# Revit family: pefy-p22_36mlg9(-r)_50Hz
name_source: partatom
category: 機械設備
units: mm (PartAtom-declared; Revit-internal decimal feet)

## family parameters
OmniClass タイトル = Split System Air Conditioning Units
OmniClass 番号 = 23.75.10.24.21.27.27
パーツ タイプ = 標準
ロード時にボイドで切り取り = いいえ
丸型コネクタ寸法 = 直径を使用
作業面ベース = いいえ
共有 = いいえ
常に垂直 = はい
部屋計算ポイント = はい

## types (6) — shared parameters
Depth = 550  [stored 1.80446 ft]
Height = 300  [stored 0.984252 ft]
IfcExportAs = IfcUnitaryEquipmentType
IfcExportType = AIRCONDITIONINGUNIT
MID風量 = 348.0 m³/h
MIN風量 = 288.0 m³/h
OmniClassCode = 23-33 17 13 11
URL = https://www.mitsubishielectric.co.jp
Uniclass2015Code = Pr_70_65_03_84
Uniclass2015Title = Split coil remote air cooled condensing units
Uniclass2015Version = Systems v1.9
Width = 530  [stored 1.73885 ft]
ドレン管径 = 27.20 mm
仕様書バージョン = Version1.0
企業コード = 108420
冷媒ガス管径 = 12.70 mm
冷媒液管径 = 6.35 mm
冷媒管径 = 100.00 mm
冷媒管径符号 = Ac
冷媒高低圧ガス管径 = 0.00 mm
分類コード = 50053003221070
加湿給水管径 = 0.00 mm
参照している仕様書等のバージョン = 公共建築工事標準仕様書（機械設備工事編）平成31年度版
周波数 = 50 Hz
呼称 = 室内機_天井吊(隠ぺい)形(両ダクト形)
始動方式 = 直入
形式 = 天井吊（隠ぺい）形（両ダクト形）
本体マテリアル = <カテゴリ別>
極数 = 1
機外静圧 = 5.0 Pa
法定耐用年数 = 15
消費電力_加湿器 = 0 W
消費電力_電気ヒーター = 0 W
相 = 1
相_電気ヒーター = 1
積算_科目 = 1 空気調和設備
符号 = ACP-CID
製品リリース年月 = 2022年9月15日
製品出荷対象 = 国内
製品質量 = 18.00 kg
製造元 = 三菱電機株式会社
設置方法 = 天井吊(隠ぺい)形
説明 = ビル用マルチエアコン 室内ユニット 天井埋込形
負荷分類 = 10_ファンコイル類
質量 = 21.60 kg
運転質量 = 0.00 kg
電圧 = 200 V
電圧_電気ヒーター = 0 V
風量（中）（m3／min） = 5.8
風量（弱）（m3／min） = 4.8
zero-valued in all types: 価格, 有効加湿量

## per-type parameters (varying)
| type | MAX風量 | R-表示 | 冷房能力 | 暖房能力 | 消費電力 | 消費電力_冷房 | 消費電力_暖房 | 表示 | 電動機出力_送風機 | 音響パワーレベル(dB) | 風量 | 風量（m3／min） | 騒音レベル（中）(dB) | 騒音レベル（弱）(dB) |
| PEFY-P22MLG9 | 474.0 m³/h | いいえ | 2 kW | 3 kW | 60 W | 60 W | 60 W | はい | 23 W | 49 | 474.0 m³/h | 7.9 | 46 | 44 |
| PEFY-P22MLG9-R | 474.0 m³/h | はい | 2 kW | 3 kW | 60 W | 60 W | 60 W | いいえ | 23 W | 49 | 474.0 m³/h | 7.9 | 46 | 44 |
| PEFY-P28MLG9 | 474.0 m³/h | いいえ | 3 kW | 3 kW | 60 W | 60 W | 60 W | はい | 23 W | 50 | 474.0 m³/h | 7.9 | 46 | 45 |
| PEFY-P28MLG9-R | 474.0 m³/h | はい | 3 kW | 3 kW | 60 W | 60 W | 60 W | いいえ | 23 W | 50 | 474.0 m³/h | 7.9 | 46 | 45 |
| PEFY-P36MLG9 | 558.0 m³/h | いいえ | 4 kW | 4 kW | 80 W | 80 W | 80 W | はい | 28 W | 53 | 558.0 m³/h | 9.3 | 47 | 46 |
| PEFY-P36MLG9-R | 558.0 m³/h | はい | 4 kW | 4 kW | 80 W | 80 W | 80 W | いいえ | 28 W | 53 | 558.0 m³/h | 9.3 | 47 | 46 |

note: column(s) folded — value = type name in every type: モデル

note: [stored X ft] marks values corroborated as IEEE doubles in the binary element streams (Revit-internal decimal feet)
